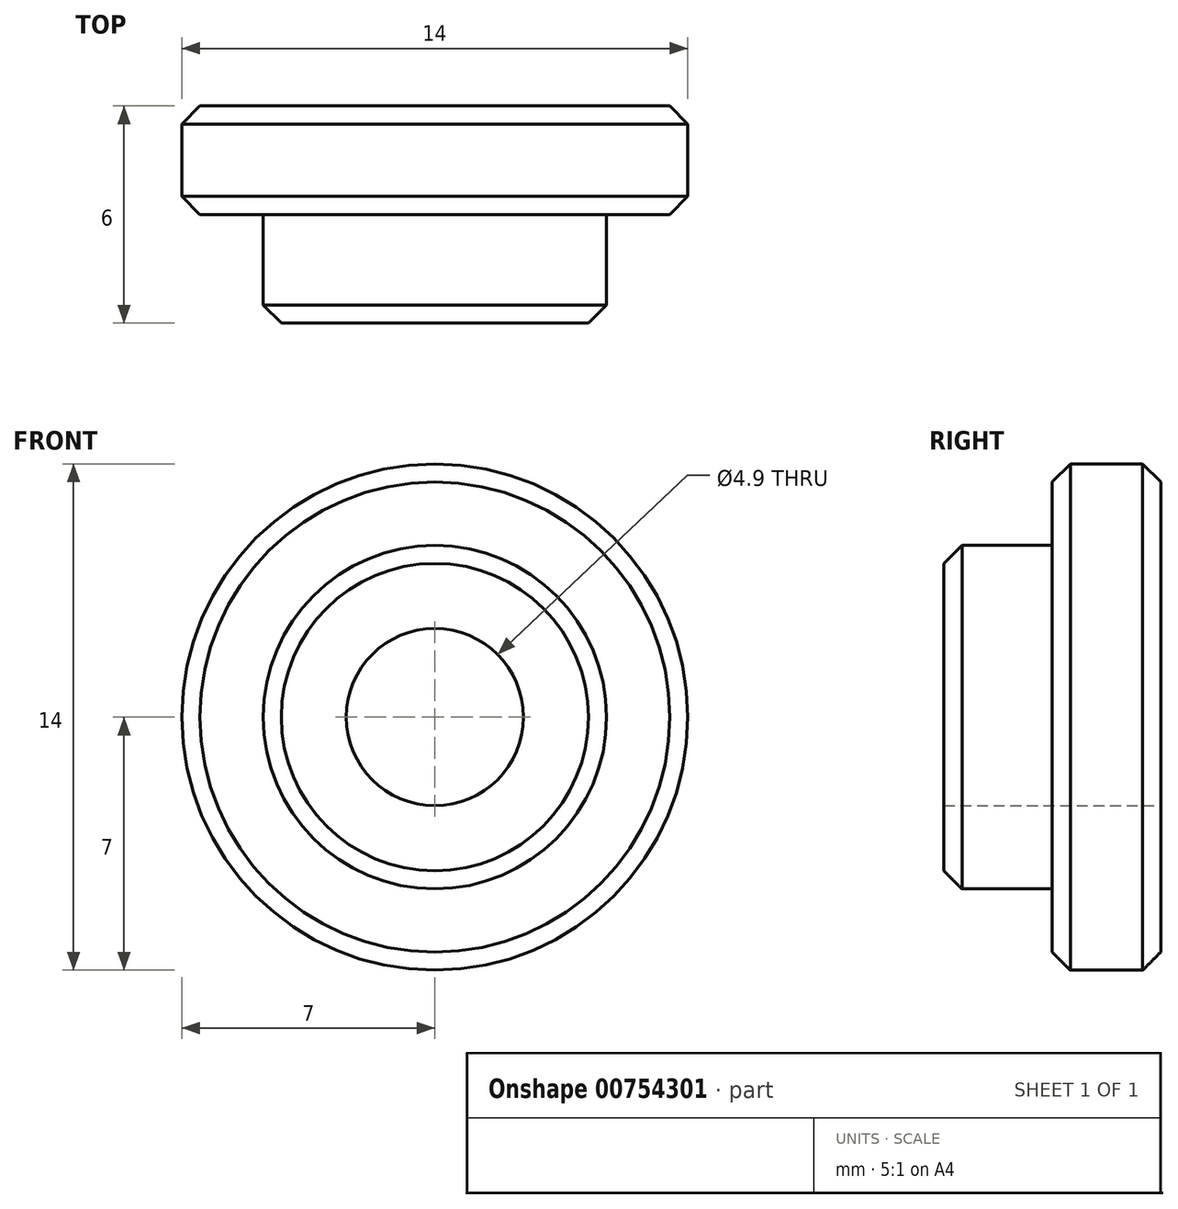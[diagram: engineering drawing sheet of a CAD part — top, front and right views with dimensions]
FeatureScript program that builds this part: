
annotation { "Feature Type Name" : "Feature", "Feature Type Description" : "" }
export const myFeature = defineFeature(function(context is Context, id is Id, definition is map)
    precondition{}
    {
        {
            var Q0;
            Q0=qCreatedBy(makeId("Front.planeOp"),FACE);
            var sketch = newSketch(context, id + "F0", { "sketchPlane" : qUnion([Q0])});
            skCircle(sketch, "E0", {"center": v(0, 0) * mm, "radius": 7 * mm});
            skCircle(sketch, "E1", {"center": v(0, 0) * mm, "radius": 4.75 * mm});
            skCircle(sketch, "E2", {"center": v(0, 0) * mm, "radius": 2.45 * mm});
            skSolve(sketch);
        }
        {
            var Q0;
            Q0=makeQuery(id+"F0.imprint","IMPRINT",FACE,{"disambiguationData":[TD([[makeQuery(id+"F0.imprint","IMPRINT",EDGE,{"derivedFrom":sQuery(id+"F0.wireOp",EDGE,"E1")}),1.0]])]});
            extrude(context, id + "F1", {"entities" : qUnion([Q0]), "depth" : 3 * mm, "offsetDistance" : 25 * mm, "hasSecondDirection" : true, "secondDirectionOppositeDirection" : true, "secondDirectionDepth" : 3 * mm});
        }
        {
            var Q0;
            Q0=makeQuery(id+"F0.imprint","IMPRINT",FACE,{"disambiguationData":[TD([[makeQuery(id+"F0.imprint","IMPRINT",EDGE,{"derivedFrom":sQuery(id+"F0.wireOp",EDGE,"E0")}),1.0]])]});
            extrude(context, id + "F2", {"entities" : qUnion([Q0]), "operationType" : NewBodyOperationType.ADD, "oppositeDirection" : true, "depth" : 3 * mm, "offsetDistance" : 25 * mm});
        }
        {
            var Q0;
            Q0=makeQuery(id+"F1.opExtrude","CAP_EDGE",EDGE,{"disambiguationData":[OSD([sQuery(id+"F0.wireOp",EDGE,"E1")])],"isStart":false});
            var Q1;
            Q1=makeQuery(id+"F2.opExtrude","CAP_EDGE",EDGE,{"disambiguationData":[OSD([sQuery(id+"F0.wireOp",EDGE,"E0")])],"isStart":true});
            var Q2;
            Q2=makeQuery(id+"F2.opExtrude","CAP_EDGE",EDGE,{"disambiguationData":[OSD([sQuery(id+"F0.wireOp",EDGE,"E0")])],"isStart":false});
            chamfer(context, id + "F3", {"entities" : qUnion([Q0, Q1, Q2]), "width" : .5 * mm, "tangentPropagation" : true});
        }
    });
